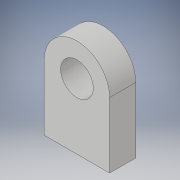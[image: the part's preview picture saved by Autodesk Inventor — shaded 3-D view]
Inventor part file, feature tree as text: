
AUTODESK INVENTOR PART (.ipt)
format: ipt  version: 2019.4 (Build 234330000, 330)  size: 102,400 bytes
history: native  units: mm
features: extrude x1, sketch x1
ambient origin geometry x8: Origin, YZ Plane, XZ Plane, XY Plane, X Axis, Y Axis, Z Axis, Center Point
bodies: Body1 (feature_tree)
feature tree (2):
  extrude  "Extrusión2"  Depth=250.0mm
  sketch  "Boceto2"  dims[d7=500.0mm d8=250.0mm d9=500.0mm d10=500.0mm d11=200.0mm d12=0.0mm]
